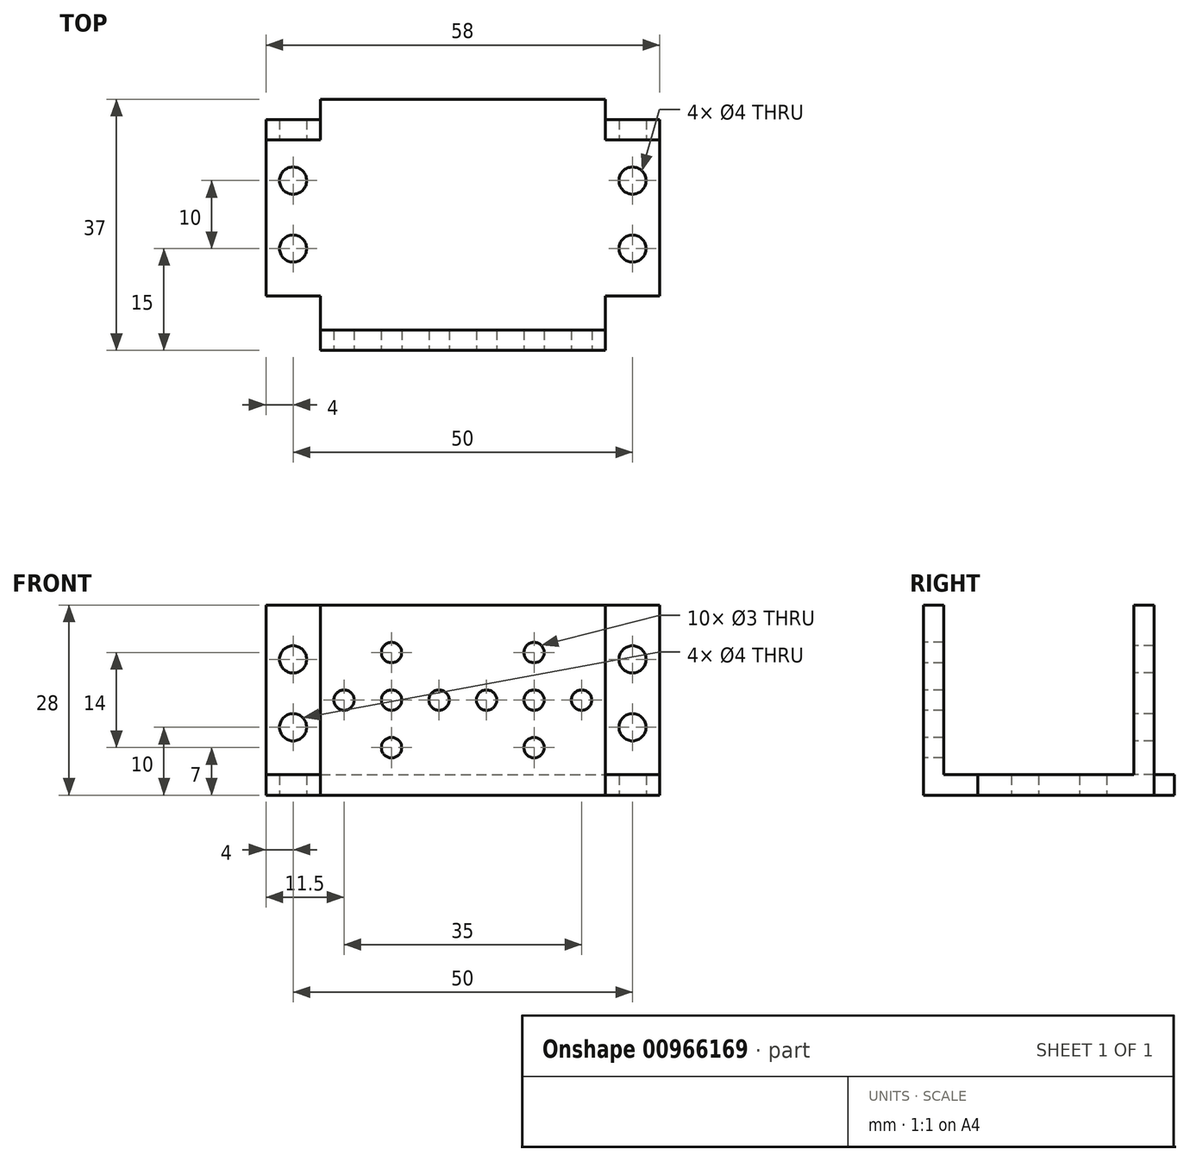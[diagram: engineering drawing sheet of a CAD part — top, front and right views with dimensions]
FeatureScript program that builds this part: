
annotation { "Feature Type Name" : "Feature", "Feature Type Description" : "" }
export const myFeature = defineFeature(function(context is Context, id is Id, definition is map)
    precondition{}
    {
        {
            var Q0;
            Q0=qCreatedBy(makeId("Top.planeOp"),FACE);
            var sketch = newSketch(context, id + "F0", { "sketchPlane" : qUnion([Q0])});
            skLineSegment(sketch, "E0.bottom", {"start": v(0, 0) * mm, "end": v(58, 0) * mm});
            skLineSegment(sketch, "E0.top", {"start": v(0, 37) * mm, "end": v(58, 37) * mm});
            skLineSegment(sketch, "E0.left", {"start": v(0, 0) * mm, "end": v(0, 37) * mm});
            skLineSegment(sketch, "E0.right", {"start": v(58, 0) * mm, "end": v(58, 37) * mm});
            skLineSegment(sketch, "E1", {"start": v(8, 0) * mm, "end": v(8, 8) * mm});
            skLineSegment(sketch, "E2", {"start": v(8, 8) * mm, "end": v(0, 8) * mm});
            skLineSegment(sketch, "E3.bottom", {"start": v(0, 37) * mm, "end": v(8, 37) * mm});
            skLineSegment(sketch, "E3.top", {"start": v(0, 34) * mm, "end": v(8, 34) * mm});
            skLineSegment(sketch, "E3.left", {"start": v(0, 37) * mm, "end": v(0, 34) * mm});
            skLineSegment(sketch, "E3.right", {"start": v(8, 37) * mm, "end": v(8, 34) * mm});
            skLineSegment(sketch, "E4", {"start": v(29, 0) * mm, "end": v(29, 37) * mm, "construction": true});
            skLineSegment(sketch, "E5.MirrorCS", {"start": v(50, 37) * mm, "end": v(50, 34) * mm});
            skLineSegment(sketch, "E6.MirrorCS", {"start": v(58, 34) * mm, "end": v(50, 34) * mm});
            skLineSegment(sketch, "E7.MirrorCS", {"start": v(50, 8) * mm, "end": v(58, 8) * mm});
            skLineSegment(sketch, "E8.MirrorCS", {"start": v(50, 0) * mm, "end": v(50, 8) * mm});
            skSolve(sketch);
        }
        {
            var Q0;
            {var subQ4=sQuery(id+"F0.wireOp",EDGE,"E1");Q0=makeQuery(id+"F0.imprint","IMPRINT",FACE,{"disambiguationData":[TD([[makeQuery(id+"F0.imprint","IMPRINT",EDGE,{"derivedFrom":subQ4}),-1.0]])]});}
            extrude(context, id + "F1", {"entities" : qUnion([Q0]), "depth" : 3 * mm, "offsetDistance" : 25 * mm});
        }
        {
            var Q0;
            Q0=makeQuery(id+"F1.opExtrude","CAP_FACE",FACE,{"disambiguationData":[OSD([sQuery(id+"F0.wireOp",EDGE,"E0.bottom"),sQuery(id+"F0.wireOp",EDGE,"E0.top"),sQuery(id+"F0.wireOp",EDGE,"E0.left"),sQuery(id+"F0.wireOp",EDGE,"E0.right"),sQuery(id+"F0.wireOp",EDGE,"E1"),sQuery(id+"F0.wireOp",EDGE,"E2"),sQuery(id+"F0.wireOp",EDGE,"E3.top"),sQuery(id+"F0.wireOp",EDGE,"E3.right"),sQuery(id+"F0.wireOp",EDGE,"E5.MirrorCS"),sQuery(id+"F0.wireOp",EDGE,"E6.MirrorCS"),sQuery(id+"F0.wireOp",EDGE,"E7.MirrorCS"),sQuery(id+"F0.wireOp",EDGE,"E8.MirrorCS")])],"isStart":false});
            var sketch = newSketch(context, id + "F2", { "sketchPlane" : qUnion([Q0])});
            skLineSegment(sketch, "E9.bottom", {"start": v(8, 0) * mm, "end": v(50, 0) * mm});
            skLineSegment(sketch, "E9.top", {"start": v(8, 3) * mm, "end": v(50, 3) * mm});
            skLineSegment(sketch, "E9.left", {"start": v(8, 0) * mm, "end": v(8, 3) * mm});
            skLineSegment(sketch, "E9.right", {"start": v(50, 0) * mm, "end": v(50, 3) * mm});
            skLineSegment(sketch, "E10.bottom", {"start": v(0, 34) * mm, "end": v(8, 34) * mm});
            skLineSegment(sketch, "E10.top", {"start": v(0, 31) * mm, "end": v(8, 31) * mm});
            skLineSegment(sketch, "E10.left", {"start": v(0, 34) * mm, "end": v(0, 31) * mm});
            skLineSegment(sketch, "E10.right", {"start": v(8, 34) * mm, "end": v(8, 31) * mm});
            skLineSegment(sketch, "E11.bottom", {"start": v(58, 34) * mm, "end": v(50, 34) * mm});
            skLineSegment(sketch, "E11.top", {"start": v(58, 31) * mm, "end": v(50, 31) * mm});
            skLineSegment(sketch, "E11.left", {"start": v(58, 34) * mm, "end": v(58, 31) * mm});
            skLineSegment(sketch, "E11.right", {"start": v(50, 34) * mm, "end": v(50, 31) * mm});
            skSolve(sketch);
        }
        {
            var Q0;
            Q0=qSketchRegion(id+"F2",true);
            extrude(context, id + "F3", {"entities" : qUnion([Q0]), "operationType" : NewBodyOperationType.ADD, "depth" : 25 * mm, "offsetDistance" : 25 * mm});
        }
        {
            var Q0;
            Q0=qCreatedBy(makeId("Front.planeOp"),FACE);
            var sketch = newSketch(context, id + "F4", { "sketchPlane" : qUnion([Q0])});
            skCircle(sketch, "E12", {"center": v(54, 20) * mm, "radius": 2 * mm});
            skCircle(sketch, "E13", {"center": v(54, 10) * mm, "radius": 2 * mm});
            skCircle(sketch, "E14", {"center": v(4, 20) * mm, "radius": 2 * mm});
            skCircle(sketch, "E15", {"center": v(4, 10) * mm, "radius": 2 * mm});
            skSolve(sketch);
        }
        {
            var Q0;
            Q0=qSketchRegion(id+"F4",true);
            extrude(context, id + "F5", {"entities" : qUnion([Q0]), "operationType" : NewBodyOperationType.REMOVE, "endBound" : BoundingType.THROUGH_ALL, "oppositeDirection" : true, "depth" : 25 * mm, "offsetDistance" : 25 * mm});
        }
        {
            var Q0;
            Q0=makeQuery(id+"F3.boolean.opBoolean","MERGE",FACE,{"derivedFrom":[makeQuery(id+"F1.opExtrude","SWEPT_FACE",FACE,{"disambiguationData":[OSD([sQuery(id+"F0.wireOp",EDGE,"E0.bottom")])]}),makeQuery(id+"F3.opExtrude","SWEPT_FACE",FACE,{"disambiguationData":[OSD([sQuery(id+"F2.wireOp",EDGE,"E9.bottom")])]})]});
            var sketch = newSketch(context, id + "F6", { "sketchPlane" : qUnion([Q0])});
            skCircle(sketch, "E16", {"center": v(39.5, 14) * mm, "radius": 1.5 * mm});
            skPoint(sketch, "E16.centerSnap0", {"position": v(50, 14) * mm});
            skCircle(sketch, "E17", {"center": v(39.5, 21) * mm, "radius": 1.5 * mm});
            skCircle(sketch, "E18.1.0.0", {"center": v(32.5, 14) * mm, "radius": 1.5 * mm});
            skCircle(sketch, "E18.2.0.0", {"center": v(25.5, 14) * mm, "radius": 1.5 * mm});
            skCircle(sketch, "E18.3.0.0", {"center": v(18.5, 14) * mm, "radius": 1.5 * mm});
            skCircle(sketch, "E18.4.0.0", {"center": v(11.5, 14) * mm, "radius": 1.5 * mm});
            skLineSegment(sketch, "E18.direction1", {"start": v(39.5, 14) * mm, "end": v(32.5, 14) * mm, "construction": true});
            skCircle(sketch, "E19", {"center": v(46.5, 14) * mm, "radius": 1.5 * mm});
            skCircle(sketch, "E20", {"center": v(18.5, 21) * mm, "radius": 1.5 * mm});
            skCircle(sketch, "E21", {"center": v(39.5, 7) * mm, "radius": 1.5 * mm});
            skCircle(sketch, "E22", {"center": v(18.5, 7) * mm, "radius": 1.5 * mm});
            skSolve(sketch);
        }
        {
            var Q0;
            Q0=qSketchRegion(id+"F6",true);
            extrude(context, id + "F7", {"entities" : qUnion([Q0]), "operationType" : NewBodyOperationType.REMOVE, "endBound" : BoundingType.THROUGH_ALL, "oppositeDirection" : true, "depth" : 25 * mm, "offsetDistance" : 25 * mm});
        }
        {
            var Q0;
            Q0=makeQuery(id+"F1.opExtrude","CAP_FACE",FACE,{"disambiguationData":[OSD([sQuery(id+"F0.wireOp",EDGE,"E0.bottom"),sQuery(id+"F0.wireOp",EDGE,"E0.top"),sQuery(id+"F0.wireOp",EDGE,"E0.left"),sQuery(id+"F0.wireOp",EDGE,"E0.right"),sQuery(id+"F0.wireOp",EDGE,"E1"),sQuery(id+"F0.wireOp",EDGE,"E2"),sQuery(id+"F0.wireOp",EDGE,"E3.top"),sQuery(id+"F0.wireOp",EDGE,"E3.right"),sQuery(id+"F0.wireOp",EDGE,"E5.MirrorCS"),sQuery(id+"F0.wireOp",EDGE,"E6.MirrorCS"),sQuery(id+"F0.wireOp",EDGE,"E7.MirrorCS"),sQuery(id+"F0.wireOp",EDGE,"E8.MirrorCS")])],"isStart":true});
            var sketch = newSketch(context, id + "F8", { "sketchPlane" : qUnion([Q0])});
            skCircle(sketch, "E23", {"center": v(4, -15) * mm, "radius": 2 * mm});
            skCircle(sketch, "E24", {"center": v(4, -25) * mm, "radius": 2 * mm});
            skCircle(sketch, "E25", {"center": v(54, -25) * mm, "radius": 2 * mm});
            skCircle(sketch, "E26", {"center": v(54, -15) * mm, "radius": 2 * mm});
            skSolve(sketch);
        }
        {
            var Q0;
            Q0=qSketchRegion(id+"F8",true);
            extrude(context, id + "F9", {"entities" : qUnion([Q0]), "operationType" : NewBodyOperationType.REMOVE, "endBound" : BoundingType.THROUGH_ALL, "oppositeDirection" : true, "depth" : 25 * mm, "offsetDistance" : 25 * mm});
        }
    });
